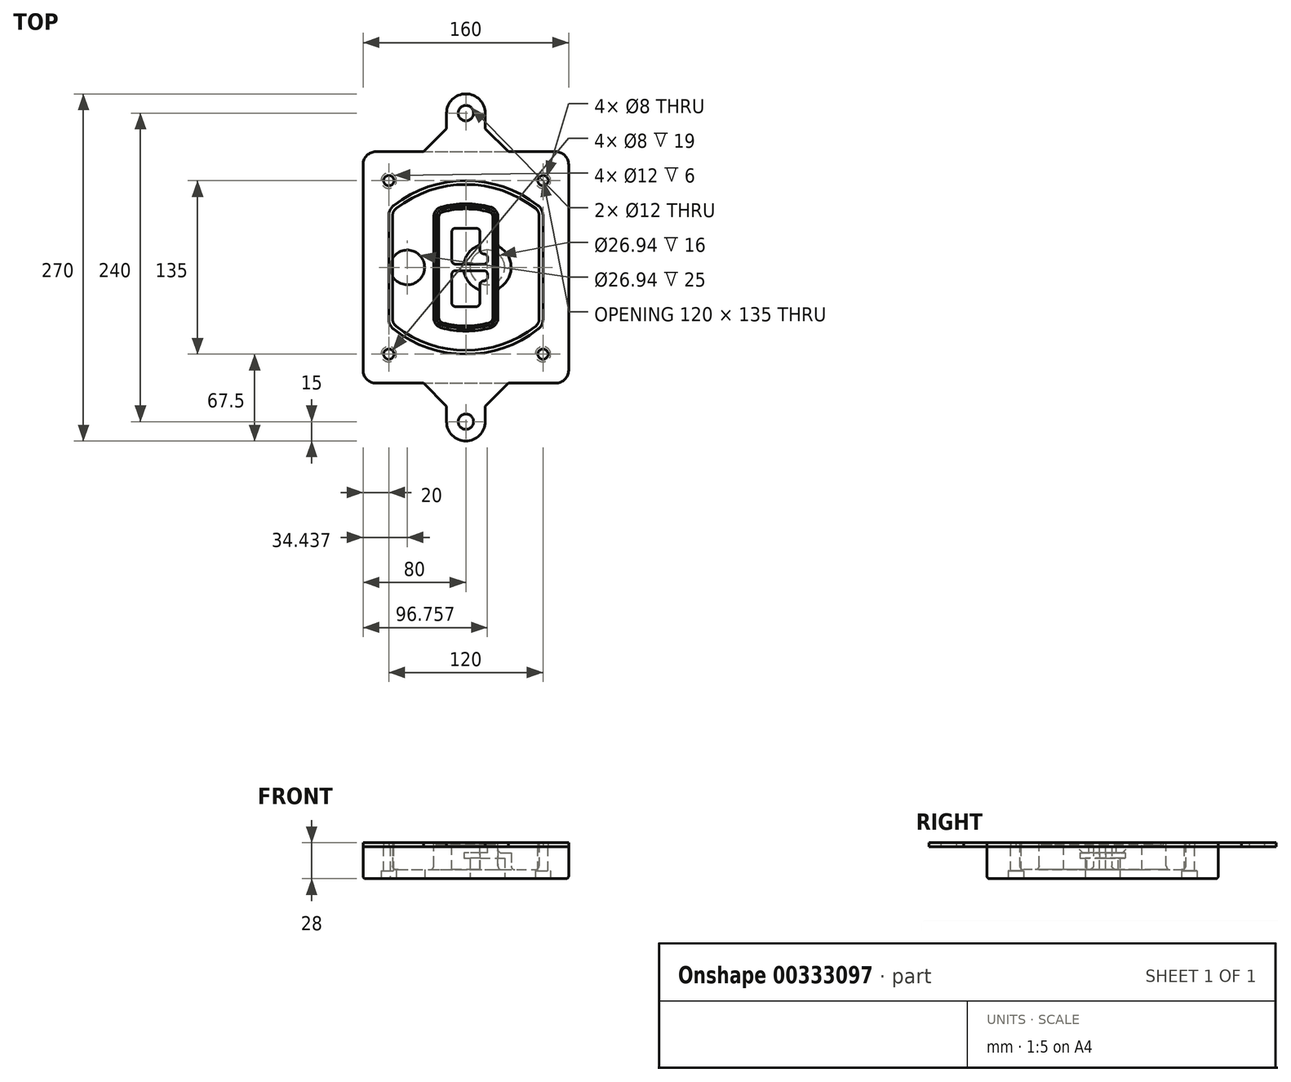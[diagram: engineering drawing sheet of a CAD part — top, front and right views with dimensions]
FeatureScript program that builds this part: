
annotation { "Feature Type Name" : "Feature", "Feature Type Description" : "" }
export const myFeature = defineFeature(function(context is Context, id is Id, definition is map)
    precondition{}
    {
        {
            var Q0;
            Q0=qCreatedBy(makeId("Top.planeOp"),FACE);
            var sketch = newSketch(context, id + "F0", { "sketchPlane" : qUnion([Q0])});
            skPoint(sketch, "E0.rect.middle", {"position": v(0, 0) * mm});
            skLineSegment(sketch, "E1.bottom", {"start": v(-70, -90) * mm, "end": v(70, -90) * mm});
            skLineSegment(sketch, "E1.top", {"start": v(-70, 90) * mm, "end": v(70, 90) * mm});
            skLineSegment(sketch, "E1.left", {"start": v(-80, -80) * mm, "end": v(-80, 80) * mm});
            skLineSegment(sketch, "E1.right", {"start": v(80, -80) * mm, "end": v(80, 80) * mm});
            skLineSegment(sketch, "E2", {"start": v(-80, 90) * mm, "end": v(80, -90) * mm, "construction": true});
            skLineSegment(sketch, "E3", {"start": v(80, 90) * mm, "end": v(-80, -90) * mm, "construction": true});
            skCircle(sketch, "E4", {"center": v(-60, 67.5) * mm, "radius": 4 * mm});
            skCircle(sketch, "E5", {"center": v(60, 67.5) * mm, "radius": 4 * mm});
            skCircle(sketch, "E6", {"center": v(60, -67.5) * mm, "radius": 4 * mm});
            skCircle(sketch, "E7", {"center": v(-60, -67.5) * mm, "radius": 4 * mm});
            skLineSegment(sketch, "E8", {"start": v(-60, 67.5) * mm, "end": v(60, 67.5) * mm, "construction": true});
            skLineSegment(sketch, "E9", {"start": v(60, 67.5) * mm, "end": v(60, -67.5) * mm, "construction": true});
            skLineSegment(sketch, "E10", {"start": v(60, -67.5) * mm, "end": v(-60, -67.5) * mm, "construction": true});
            skLineSegment(sketch, "E11", {"start": v(-60, -67.5) * mm, "end": v(-60, 67.5) * mm, "construction": true});
            skLineSegment(sketch, "E12", {"start": v(-60, 40.3) * mm, "end": v(-60, -40.3) * mm});
            skLineSegment(sketch, "E13", {"start": v(60, 40.3) * mm, "end": v(60, -40.3) * mm});
            skArc(sketch, "E14", {"start": v(56.15, 48.18) * mm, "mid": v(0, 67.5) * mm, "end": v(-56.15, 48.18) * mm});
            skArc(sketch, "E15", {"start": v(-56.15, -48.18) * mm, "mid": v(0, -67.5) * mm, "end": v(56.15, -48.18) * mm});
            skLineSegment(sketch, "E16", {"start": v(-60, 0) * mm, "end": v(60, 0) * mm, "construction": true});
            skPoint(sketch, "E17.visualSharp", {"position": v(-60, -45) * mm});
            skArc(sketch, "E17.filletArc", {"start": v(-60, -40.3) * mm, "mid": v(-58.99, -44.68) * mm, "end": v(-56.15, -48.18) * mm});
            skPoint(sketch, "E18.visualSharp", {"position": v(-60, 45) * mm});
            skArc(sketch, "E18.filletArc", {"start": v(-56.15, 48.18) * mm, "mid": v(-58.99, 44.68) * mm, "end": v(-60, 40.3) * mm});
            skPoint(sketch, "E19.visualSharp", {"position": v(60, 45) * mm});
            skArc(sketch, "E19.filletArc", {"start": v(60, 40.3) * mm, "mid": v(58.99, 44.68) * mm, "end": v(56.15, 48.18) * mm});
            skPoint(sketch, "E20.visualSharp", {"position": v(60, -45) * mm});
            skArc(sketch, "E20.filletArc", {"start": v(56.15, -48.18) * mm, "mid": v(58.99, -44.68) * mm, "end": v(60, -40.3) * mm});
            skPoint(sketch, "E21.visualSharp", {"position": v(-80, 90) * mm});
            skArc(sketch, "E21.filletArc", {"start": v(-70, 90) * mm, "mid": v(-77.07, 87.07) * mm, "end": v(-80, 80) * mm});
            skPoint(sketch, "E22.visualSharp", {"position": v(80, 90) * mm});
            skArc(sketch, "E22.filletArc", {"start": v(80, 80) * mm, "mid": v(77.07, 87.07) * mm, "end": v(70, 90) * mm});
            skPoint(sketch, "E23.visualSharp", {"position": v(80, -90) * mm});
            skArc(sketch, "E23.filletArc", {"start": v(70, -90) * mm, "mid": v(77.07, -87.07) * mm, "end": v(80, -80) * mm});
            skPoint(sketch, "E24.visualSharp", {"position": v(-80, -90) * mm});
            skArc(sketch, "E24.filletArc", {"start": v(-80, -80) * mm, "mid": v(-77.07, -87.07) * mm, "end": v(-70, -90) * mm});
            skArc(sketch, "E25.0", {"start": v(57, 40.3) * mm, "mid": v(56.3, 43.36) * mm, "end": v(54.3, 45.81) * mm});
            skLineSegment(sketch, "E25.1", {"start": v(57, 40.3) * mm, "end": v(57, -40.3) * mm});
            skArc(sketch, "E25.2", {"start": v(54.3, -45.81) * mm, "mid": v(56.3, -43.36) * mm, "end": v(57, -40.3) * mm});
            skArc(sketch, "E25.3", {"start": v(-54.3, -45.81) * mm, "mid": v(0, -64.5) * mm, "end": v(54.3, -45.81) * mm});
            skArc(sketch, "E25.4", {"start": v(-57, -40.3) * mm, "mid": v(-56.3, -43.36) * mm, "end": v(-54.3, -45.81) * mm});
            skArc(sketch, "E25.5", {"start": v(54.3, 45.81) * mm, "mid": v(0, 64.5) * mm, "end": v(-54.3, 45.81) * mm});
            skLineSegment(sketch, "E25.6", {"start": v(-57, 40.3) * mm, "end": v(-57, -40.3) * mm});
            skArc(sketch, "E25.7", {"start": v(-54.3, 45.81) * mm, "mid": v(-56.3, 43.36) * mm, "end": v(-57, 40.3) * mm});
            skArc(sketch, "E26.0", {"start": v(-58.62, 51.33) * mm, "mid": v(-62.58, 46.43) * mm, "end": v(-64, 40.3) * mm});
            skArc(sketch, "E26.1", {"start": v(58.62, 51.33) * mm, "mid": v(0, 71.5) * mm, "end": v(-58.62, 51.33) * mm});
            skArc(sketch, "E26.2", {"start": v(64, 40.3) * mm, "mid": v(62.58, 46.43) * mm, "end": v(58.62, 51.33) * mm});
            skLineSegment(sketch, "E26.3", {"start": v(64, 40.3) * mm, "end": v(64, -40.3) * mm});
            skArc(sketch, "E26.4", {"start": v(58.62, -51.33) * mm, "mid": v(62.58, -46.43) * mm, "end": v(64, -40.3) * mm});
            skLineSegment(sketch, "E26.5", {"start": v(-64, 40.3) * mm, "end": v(-64, -40.3) * mm});
            skArc(sketch, "E26.6", {"start": v(-58.62, -51.33) * mm, "mid": v(0, -71.5) * mm, "end": v(58.62, -51.33) * mm});
            skArc(sketch, "E26.7", {"start": v(-64, -40.3) * mm, "mid": v(-62.58, -46.43) * mm, "end": v(-58.62, -51.33) * mm});
            skSolve(sketch);
        }
        {
            var Q0;
            Q0=makeQuery(id+"F0.imprint","IMPRINT",FACE,{"disambiguationData":[TD([[makeQuery(id+"F0.imprint","IMPRINT",EDGE,{"derivedFrom":sQuery(id+"F0.wireOp",EDGE,"E1.bottom")}),1.0]])]});
            var Q1;
            Q1=makeQuery(id+"F0.imprint","IMPRINT",FACE,{"disambiguationData":[TD([[makeQuery(id+"F0.imprint","IMPRINT",EDGE,{"derivedFrom":sQuery(id+"F0.wireOp",EDGE,"E12")}),1.0]])]});
            var Q2;
            Q2=makeQuery(id+"F0.imprint","IMPRINT",FACE,{"disambiguationData":[TD([[makeQuery(id+"F0.imprint","IMPRINT",EDGE,{"derivedFrom":sQuery(id+"F0.wireOp",EDGE,"E25.0")}),1.0]])]});
            var Q3;
            Q3=makeQuery(id+"F0.imprint","IMPRINT",FACE,{"disambiguationData":[TD([[makeQuery(id+"F0.imprint","IMPRINT",EDGE,{"derivedFrom":sQuery(id+"F0.wireOp",EDGE,"E12")}),-1.0]])]});
            extrude(context, id + "F1", {"entities" : qUnion([Q0, Q1, Q2, Q3]), "oppositeDirection" : true, "depth" : 25 * mm});
        }
        {
            var Q0;
            Q0=makeQuery(id+"F0.imprint","IMPRINT",FACE,{"disambiguationData":[TD([[makeQuery(id+"F0.imprint","IMPRINT",EDGE,{"derivedFrom":sQuery(id+"F0.wireOp",EDGE,"E12")}),1.0]])]});
            extrude(context, id + "F2", {"entities" : qUnion([Q0]), "operationType" : NewBodyOperationType.ADD, "depth" : 3 * mm});
        }
        {
            var Q0;
            Q0=makeQuery(id+"F0.imprint","IMPRINT",FACE,{"disambiguationData":[TD([[makeQuery(id+"F0.imprint","IMPRINT",EDGE,{"derivedFrom":sQuery(id+"F0.wireOp",EDGE,"E25.0")}),1.0]])]});
            extrude(context, id + "F3", {"entities" : qUnion([Q0]), "operationType" : NewBodyOperationType.REMOVE, "oppositeDirection" : true, "depth" : 18 * mm});
        }
        {
            var Q0;
            Q0=makeQuery(id+"F2.opExtrude","CAP_FACE",FACE,{"disambiguationData":[OSD([sQuery(id+"F0.wireOp",EDGE,"E12"),sQuery(id+"F0.wireOp",EDGE,"E13"),sQuery(id+"F0.wireOp",EDGE,"E14"),sQuery(id+"F0.wireOp",EDGE,"E15"),sQuery(id+"F0.wireOp",EDGE,"E17.filletArc"),sQuery(id+"F0.wireOp",EDGE,"E18.filletArc"),sQuery(id+"F0.wireOp",EDGE,"E19.filletArc"),sQuery(id+"F0.wireOp",EDGE,"E20.filletArc"),sQuery(id+"F0.wireOp",EDGE,"E25.0"),sQuery(id+"F0.wireOp",EDGE,"E25.1"),sQuery(id+"F0.wireOp",EDGE,"E25.2"),sQuery(id+"F0.wireOp",EDGE,"E25.3"),sQuery(id+"F0.wireOp",EDGE,"E25.4"),sQuery(id+"F0.wireOp",EDGE,"E25.5"),sQuery(id+"F0.wireOp",EDGE,"E25.6"),sQuery(id+"F0.wireOp",EDGE,"E25.7")])],"isStart":false});
            var sketch = newSketch(context, id + "F4", { "sketchPlane" : qUnion([Q0])});
            skArc(sketch, "E27.0", {"start": v(-19.08, -46.97) * mm, "mid": v(0, -49.5) * mm, "end": v(19.08, -46.97) * mm});
            skArc(sketch, "E28.0", {"start": v(19.08, 46.97) * mm, "mid": v(0, 49.5) * mm, "end": v(-19.08, 46.97) * mm});
            skLineSegment(sketch, "E29", {"start": v(-25, 39.25) * mm, "end": v(-25, -39.25) * mm});
            skLineSegment(sketch, "E30", {"start": v(25, 39.25) * mm, "end": v(25, -39.25) * mm});
            skLineSegment(sketch, "E31", {"start": v(-25, 45.1) * mm, "end": v(25, 45.1) * mm, "construction": true});
            skLineSegment(sketch, "E32", {"start": v(-25, -45.1) * mm, "end": v(25, -45.1) * mm, "construction": true});
            skPoint(sketch, "E33.visualSharp", {"position": v(-25, 45.1) * mm});
            skArc(sketch, "E33.filletArc", {"start": v(-19.08, 46.97) * mm, "mid": v(-23.35, 44.11) * mm, "end": v(-25, 39.25) * mm});
            skPoint(sketch, "E34.visualSharp", {"position": v(25, 45.1) * mm});
            skArc(sketch, "E34.filletArc", {"start": v(25, 39.25) * mm, "mid": v(23.35, 44.11) * mm, "end": v(19.08, 46.97) * mm});
            skPoint(sketch, "E35.visualSharp", {"position": v(25, -45.1) * mm});
            skArc(sketch, "E35.filletArc", {"start": v(19.08, -46.97) * mm, "mid": v(23.35, -44.11) * mm, "end": v(25, -39.25) * mm});
            skPoint(sketch, "E36.visualSharp", {"position": v(-25, -45.1) * mm});
            skArc(sketch, "E36.filletArc", {"start": v(-25, -39.25) * mm, "mid": v(-23.35, -44.11) * mm, "end": v(-19.08, -46.97) * mm});
            skArc(sketch, "E37.0", {"start": v(54.3, 45.81) * mm, "mid": v(0, 64.5) * mm, "end": v(-54.3, 45.81) * mm});
            skArc(sketch, "E37.1", {"start": v(-54.3, 45.81) * mm, "mid": v(-56.3, 43.36) * mm, "end": v(-57, 40.3) * mm});
            skLineSegment(sketch, "E37.2", {"start": v(-57, 40.3) * mm, "end": v(-57, -40.3) * mm});
            skArc(sketch, "E37.3", {"start": v(-57, -40.3) * mm, "mid": v(-56.3, -43.36) * mm, "end": v(-54.3, -45.81) * mm});
            skArc(sketch, "E37.4", {"start": v(-54.3, -45.81) * mm, "mid": v(0, -64.5) * mm, "end": v(54.3, -45.81) * mm});
            skArc(sketch, "E37.5", {"start": v(54.3, -45.81) * mm, "mid": v(56.3, -43.36) * mm, "end": v(57, -40.3) * mm});
            skLineSegment(sketch, "E37.6", {"start": v(57, 40.3) * mm, "end": v(57, -40.3) * mm});
            skArc(sketch, "E37.7", {"start": v(57, 40.3) * mm, "mid": v(56.3, 43.36) * mm, "end": v(54.3, 45.81) * mm});
            skLineSegment(sketch, "E38.0", {"start": v(23, 39.25) * mm, "end": v(23, -39.25) * mm});
            skArc(sketch, "E38.1", {"start": v(18.56, -45.04) * mm, "mid": v(21.76, -42.9) * mm, "end": v(23, -39.25) * mm});
            skArc(sketch, "E38.2", {"start": v(-18.56, -45.04) * mm, "mid": v(0, -47.5) * mm, "end": v(18.56, -45.04) * mm});
            skArc(sketch, "E38.3", {"start": v(-23, -39.25) * mm, "mid": v(-21.76, -42.9) * mm, "end": v(-18.56, -45.04) * mm});
            skLineSegment(sketch, "E38.4", {"start": v(-23, 39.25) * mm, "end": v(-23, -39.25) * mm});
            skArc(sketch, "E38.5", {"start": v(23, 39.25) * mm, "mid": v(21.76, 42.9) * mm, "end": v(18.56, 45.04) * mm});
            skArc(sketch, "E38.6", {"start": v(-18.56, 45.04) * mm, "mid": v(-21.76, 42.9) * mm, "end": v(-23, 39.25) * mm});
            skArc(sketch, "E38.7", {"start": v(18.56, 45.04) * mm, "mid": v(0, 47.5) * mm, "end": v(-18.56, 45.04) * mm});
            skArc(sketch, "E39.0", {"start": v(21, 39.25) * mm, "mid": v(20.18, 41.68) * mm, "end": v(18.04, 43.1) * mm});
            skLineSegment(sketch, "E39.1", {"start": v(21, 39.25) * mm, "end": v(21, -39.25) * mm});
            skArc(sketch, "E39.2", {"start": v(18.04, -43.1) * mm, "mid": v(20.18, -41.68) * mm, "end": v(21, -39.25) * mm});
            skArc(sketch, "E39.3", {"start": v(-18.04, -43.1) * mm, "mid": v(0, -45.5) * mm, "end": v(18.04, -43.1) * mm});
            skArc(sketch, "E39.4", {"start": v(-21, -39.25) * mm, "mid": v(-20.18, -41.68) * mm, "end": v(-18.04, -43.1) * mm});
            skArc(sketch, "E39.5", {"start": v(18.04, 43.1) * mm, "mid": v(0, 45.5) * mm, "end": v(-18.04, 43.1) * mm});
            skLineSegment(sketch, "E39.6", {"start": v(-21, 39.25) * mm, "end": v(-21, -39.25) * mm});
            skArc(sketch, "E39.7", {"start": v(-18.04, 43.1) * mm, "mid": v(-20.18, 41.68) * mm, "end": v(-21, 39.25) * mm});
            skLineSegment(sketch, "E40", {"start": v(-25, 0) * mm, "end": v(25, 0) * mm, "construction": true});
            skLineSegment(sketch, "E41", {"start": v(-11, 5.5) * mm, "end": v(-11, 27.5) * mm});
            skLineSegment(sketch, "E42", {"start": v(-8, 30.5) * mm, "end": v(8, 30.5) * mm});
            skLineSegment(sketch, "E43", {"start": v(11, 27.5) * mm, "end": v(11, 13.5) * mm});
            skLineSegment(sketch, "E44", {"start": v(14, 10.5) * mm, "end": v(14, 10.5) * mm});
            skLineSegment(sketch, "E45", {"start": v(17, 7.5) * mm, "end": v(17, 5.5) * mm});
            skLineSegment(sketch, "E46", {"start": v(14, 2.5) * mm, "end": v(-8, 2.5) * mm});
            skPoint(sketch, "E47.visualSharp", {"position": v(-11, 30.5) * mm});
            skArc(sketch, "E47.filletArc", {"start": v(-8, 30.5) * mm, "mid": v(-10.12, 29.62) * mm, "end": v(-11, 27.5) * mm});
            skPoint(sketch, "E48.visualSharp", {"position": v(11, 30.5) * mm});
            skArc(sketch, "E48.filletArc", {"start": v(11, 27.5) * mm, "mid": v(10.12, 29.62) * mm, "end": v(8, 30.5) * mm});
            skPoint(sketch, "E49.visualSharp", {"position": v(11, 10.5) * mm});
            skArc(sketch, "E49.filletArc", {"start": v(11, 13.5) * mm, "mid": v(11.88, 11.38) * mm, "end": v(14, 10.5) * mm});
            skPoint(sketch, "E50.visualSharp", {"position": v(17, 10.5) * mm});
            skArc(sketch, "E50.filletArc", {"start": v(17, 7.5) * mm, "mid": v(16.12, 9.62) * mm, "end": v(14, 10.5) * mm});
            skPoint(sketch, "E51.visualSharp", {"position": v(17, 2.5) * mm});
            skArc(sketch, "E51.filletArc", {"start": v(14, 2.5) * mm, "mid": v(16.12, 3.38) * mm, "end": v(17, 5.5) * mm});
            skPoint(sketch, "E52.visualSharp", {"position": v(-11, 2.5) * mm});
            skArc(sketch, "E52.filletArc", {"start": v(-11, 5.5) * mm, "mid": v(-10.12, 3.38) * mm, "end": v(-8, 2.5) * mm});
            skLineSegment(sketch, "E53.0.MirrorCS", {"start": v(14, -2.5) * mm, "end": v(-8, -2.5) * mm});
            skArc(sketch, "E54.0.MirrorCS", {"start": v(-11, -5.5) * mm, "mid": v(-10.12, -3.38) * mm, "end": v(-8, -2.5) * mm});
            skLineSegment(sketch, "E55.0.MirrorCS", {"start": v(-11, -5.5) * mm, "end": v(-11, -27.5) * mm});
            skArc(sketch, "E56.0.MirrorCS", {"start": v(-8, -30.5) * mm, "mid": v(-10.12, -29.62) * mm, "end": v(-11, -27.5) * mm});
            skLineSegment(sketch, "E57.0.MirrorCS", {"start": v(-8, -30.5) * mm, "end": v(8, -30.5) * mm});
            skArc(sketch, "E58.0.MirrorCS", {"start": v(11, -27.5) * mm, "mid": v(10.12, -29.62) * mm, "end": v(8, -30.5) * mm});
            skLineSegment(sketch, "E59.0.MirrorCS", {"start": v(11, -27.5) * mm, "end": v(11, -13.5) * mm});
            skArc(sketch, "E60.0.MirrorCS", {"start": v(11, -13.5) * mm, "mid": v(11.88, -11.38) * mm, "end": v(14, -10.5) * mm});
            skArc(sketch, "E61.0.MirrorCS", {"start": v(17, -7.5) * mm, "mid": v(16.12, -9.62) * mm, "end": v(14, -10.5) * mm});
            skLineSegment(sketch, "E62.0.MirrorCS", {"start": v(17, -7.5) * mm, "end": v(17, -5.5) * mm});
            skArc(sketch, "E63.0.MirrorCS", {"start": v(14, -2.5) * mm, "mid": v(16.12, -3.38) * mm, "end": v(17, -5.5) * mm});
            skSolve(sketch);
        }
        {
            var Q0;
            Q0=makeQuery(id+"F4.imprint","IMPRINT",FACE,{"disambiguationData":[TD([[makeQuery(id+"F4.imprint","IMPRINT",EDGE,{"derivedFrom":sQuery(id+"F4.wireOp",EDGE,"E27.0")}),1.0]])]});
            var Q1;
            Q1=makeQuery(id+"F4.imprint","IMPRINT",FACE,{"disambiguationData":[TD([[makeQuery(id+"F4.imprint","IMPRINT",EDGE,{"derivedFrom":sQuery(id+"F4.wireOp",EDGE,"E38.0")}),-1.0]])]});
            var Q2;
            Q2=makeQuery(id+"F4.imprint","IMPRINT",FACE,{"disambiguationData":[TD([[makeQuery(id+"F4.imprint","IMPRINT",EDGE,{"derivedFrom":sQuery(id+"F4.wireOp",EDGE,"E39.0")}),1.0]])]});
            extrude(context, id + "F5", {"entities" : qUnion([Q0, Q1, Q2]), "operationType" : NewBodyOperationType.ADD, "endBound" : BoundingType.UP_TO_NEXT, "oppositeDirection" : true, "depth" : 25 * mm});
        }
        {
            var Q0;
            Q0=makeQuery(id+"F4.imprint","IMPRINT",FACE,{"disambiguationData":[TD([[makeQuery(id+"F4.imprint","IMPRINT",EDGE,{"derivedFrom":sQuery(id+"F4.wireOp",EDGE,"E38.0")}),-1.0]])]});
            extrude(context, id + "F6", {"entities" : qUnion([Q0]), "operationType" : NewBodyOperationType.REMOVE, "oppositeDirection" : true, "depth" : 2 * mm});
        }
        {
            var Q0;
            Q0=makeQuery(id+"F1.opExtrude","CAP_FACE",FACE,{"disambiguationData":[OSD([sQuery(id+"F0.wireOp",EDGE,"E1.bottom"),sQuery(id+"F0.wireOp",EDGE,"E1.top"),sQuery(id+"F0.wireOp",EDGE,"E1.left"),sQuery(id+"F0.wireOp",EDGE,"E1.right"),sQuery(id+"F0.wireOp",EDGE,"E4"),sQuery(id+"F0.wireOp",EDGE,"E5"),sQuery(id+"F0.wireOp",EDGE,"E6"),sQuery(id+"F0.wireOp",EDGE,"E7"),sQuery(id+"F0.wireOp",EDGE,"E21.filletArc"),sQuery(id+"F0.wireOp",EDGE,"E22.filletArc"),sQuery(id+"F0.wireOp",EDGE,"E23.filletArc"),sQuery(id+"F0.wireOp",EDGE,"E24.filletArc")])],"isStart":false});
            var sketch = newSketch(context, id + "F7", { "sketchPlane" : qUnion([Q0])});
            skCircle(sketch, "E64", {"center": v(16.76, 0) * mm, "radius": 13.47 * mm});
            skCircle(sketch, "E65", {"center": v(-45.56, 0) * mm, "radius": 13.47 * mm});
            skLineSegment(sketch, "E66", {"start": v(80, 0) * mm, "end": v(-80, 0) * mm});
            skCircle(sketch, "E67", {"center": v(16.76, 0) * mm, "radius": 18.47 * mm});
            skCircle(sketch, "E68", {"center": v(60, -67.5) * mm, "radius": 6 * mm});
            skCircle(sketch, "E69", {"center": v(-60, -67.5) * mm, "radius": 6 * mm});
            skCircle(sketch, "E70", {"center": v(-60, 67.5) * mm, "radius": 6 * mm});
            skCircle(sketch, "E71", {"center": v(60, 67.5) * mm, "radius": 6 * mm});
            skSolve(sketch);
        }
        {
            var Q0;
            {var subQ1=sQuery(id+"F7.wireOp",EDGE,"E66");var subQ4=sQuery(id+"F7.wireOp",EDGE,"E64");var subQ6=makeQuery(id+"F7.imprint","INTERSECT",VERTEX,{"disambiguationData":[OD(0.0)],"derivedFrom":[subQ4,subQ1]});Q0=makeQuery(id+"F7.imprint","IMPRINT",FACE,{"disambiguationData":[TD([[makeQuery(id+"F7.imprint","IMPRINT",EDGE,{"disambiguationData":[TD([[subQ6,-1.0]])],"derivedFrom":subQ4}),-1.0]])]});}
            var Q1;
            {var subQ0=sQuery(id+"F7.wireOp",EDGE,"E66");var subQ1=sQuery(id+"F7.wireOp",EDGE,"E64");var subQ3=makeQuery(id+"F7.imprint","INTERSECT",VERTEX,{"disambiguationData":[OD(0.0)],"derivedFrom":[subQ1,subQ0]});Q1=makeQuery(id+"F7.imprint","IMPRINT",FACE,{"disambiguationData":[TD([[makeQuery(id+"F7.imprint","IMPRINT",EDGE,{"disambiguationData":[TD([[subQ3,-1.0]])],"derivedFrom":subQ1}),1.0]])]});}
            var Q2;
            {var subQ0=sQuery(id+"F7.wireOp",EDGE,"E66");var subQ1=sQuery(id+"F7.wireOp",EDGE,"E64");var subQ3=makeQuery(id+"F7.imprint","INTERSECT",VERTEX,{"disambiguationData":[OD(0.0)],"derivedFrom":[subQ1,subQ0]});Q2=makeQuery(id+"F7.imprint","IMPRINT",FACE,{"disambiguationData":[TD([[makeQuery(id+"F7.imprint","IMPRINT",EDGE,{"disambiguationData":[TD([[subQ3,1.0]])],"derivedFrom":subQ1}),1.0]])]});}
            var Q3;
            {var subQ1=sQuery(id+"F7.wireOp",EDGE,"E66");var subQ4=sQuery(id+"F7.wireOp",EDGE,"E64");var subQ6=makeQuery(id+"F7.imprint","INTERSECT",VERTEX,{"disambiguationData":[OD(0.0)],"derivedFrom":[subQ4,subQ1]});Q3=makeQuery(id+"F7.imprint","IMPRINT",FACE,{"disambiguationData":[TD([[makeQuery(id+"F7.imprint","IMPRINT",EDGE,{"disambiguationData":[TD([[subQ6,1.0]])],"derivedFrom":subQ4}),-1.0]])]});}
            extrude(context, id + "F8", {"entities" : qUnion([Q0, Q1, Q2, Q3]), "operationType" : NewBodyOperationType.ADD, "oppositeDirection" : true, "depth" : 20 * mm});
        }
        {
            var Q0;
            {var subQ0=sQuery(id+"F7.wireOp",EDGE,"E66");var subQ1=sQuery(id+"F7.wireOp",EDGE,"E64");var subQ3=makeQuery(id+"F7.imprint","INTERSECT",VERTEX,{"disambiguationData":[OD(0.0)],"derivedFrom":[subQ1,subQ0]});Q0=makeQuery(id+"F7.imprint","IMPRINT",FACE,{"disambiguationData":[TD([[makeQuery(id+"F7.imprint","IMPRINT",EDGE,{"disambiguationData":[TD([[subQ3,-1.0]])],"derivedFrom":subQ1}),1.0]])]});}
            var Q1;
            {var subQ0=sQuery(id+"F7.wireOp",EDGE,"E66");var subQ1=sQuery(id+"F7.wireOp",EDGE,"E64");var subQ3=makeQuery(id+"F7.imprint","INTERSECT",VERTEX,{"disambiguationData":[OD(0.0)],"derivedFrom":[subQ1,subQ0]});Q1=makeQuery(id+"F7.imprint","IMPRINT",FACE,{"disambiguationData":[TD([[makeQuery(id+"F7.imprint","IMPRINT",EDGE,{"disambiguationData":[TD([[subQ3,1.0]])],"derivedFrom":subQ1}),1.0]])]});}
            extrude(context, id + "F9", {"entities" : qUnion([Q0, Q1]), "operationType" : NewBodyOperationType.REMOVE, "oppositeDirection" : true, "depth" : 16 * mm});
        }
        {
            var Q0;
            {var subQ0=sQuery(id+"F7.wireOp",EDGE,"E66");var subQ1=sQuery(id+"F7.wireOp",EDGE,"E65");var subQ3=makeQuery(id+"F7.imprint","INTERSECT",VERTEX,{"disambiguationData":[OD(0.0)],"derivedFrom":[subQ1,subQ0]});Q0=makeQuery(id+"F7.imprint","IMPRINT",FACE,{"disambiguationData":[TD([[makeQuery(id+"F7.imprint","IMPRINT",EDGE,{"disambiguationData":[TD([[subQ3,-1.0]])],"derivedFrom":subQ1}),1.0]])]});}
            var Q1;
            {var subQ0=sQuery(id+"F7.wireOp",EDGE,"E66");var subQ1=sQuery(id+"F7.wireOp",EDGE,"E65");var subQ3=makeQuery(id+"F7.imprint","INTERSECT",VERTEX,{"disambiguationData":[OD(0.0)],"derivedFrom":[subQ1,subQ0]});Q1=makeQuery(id+"F7.imprint","IMPRINT",FACE,{"disambiguationData":[TD([[makeQuery(id+"F7.imprint","IMPRINT",EDGE,{"disambiguationData":[TD([[subQ3,1.0]])],"derivedFrom":subQ1}),1.0]])]});}
            extrude(context, id + "F10", {"entities" : qUnion([Q0, Q1]), "operationType" : NewBodyOperationType.REMOVE, "oppositeDirection" : true, "depth" : 25 * mm});
        }
        {
            var Q0;
            Q0=makeQuery(id+"F7.imprint","IMPRINT",FACE,{"disambiguationData":[TD([[makeQuery(id+"F7.imprint","IMPRINT",EDGE,{"derivedFrom":sQuery(id+"F7.wireOp",EDGE,"E68")}),1.0]])]});
            var Q1;
            Q1=makeQuery(id+"F7.imprint","IMPRINT",FACE,{"disambiguationData":[TD([[makeQuery(id+"F7.imprint","IMPRINT",EDGE,{"derivedFrom":makeQuery(id+"F1.opExtrude","CAP_EDGE",EDGE,{"disambiguationData":[OSD([sQuery(id+"F0.wireOp",EDGE,"E5")])],"isStart":false})}),-1.0]])]});
            var Q2;
            Q2=makeQuery(id+"F7.imprint","IMPRINT",FACE,{"disambiguationData":[TD([[makeQuery(id+"F7.imprint","IMPRINT",EDGE,{"derivedFrom":sQuery(id+"F7.wireOp",EDGE,"E69")}),1.0]])]});
            var Q3;
            Q3=makeQuery(id+"F7.imprint","IMPRINT",FACE,{"disambiguationData":[TD([[makeQuery(id+"F7.imprint","IMPRINT",EDGE,{"derivedFrom":makeQuery(id+"F1.opExtrude","CAP_EDGE",EDGE,{"disambiguationData":[OSD([sQuery(id+"F0.wireOp",EDGE,"E4")])],"isStart":false})}),-1.0]])]});
            var Q4;
            Q4=makeQuery(id+"F7.imprint","IMPRINT",FACE,{"disambiguationData":[TD([[makeQuery(id+"F7.imprint","IMPRINT",EDGE,{"derivedFrom":sQuery(id+"F7.wireOp",EDGE,"E70")}),1.0]])]});
            var Q5;
            Q5=makeQuery(id+"F7.imprint","IMPRINT",FACE,{"disambiguationData":[TD([[makeQuery(id+"F7.imprint","IMPRINT",EDGE,{"derivedFrom":makeQuery(id+"F1.opExtrude","CAP_EDGE",EDGE,{"disambiguationData":[OSD([sQuery(id+"F0.wireOp",EDGE,"E7")])],"isStart":false})}),-1.0]])]});
            var Q6;
            Q6=makeQuery(id+"F7.imprint","IMPRINT",FACE,{"disambiguationData":[TD([[makeQuery(id+"F7.imprint","IMPRINT",EDGE,{"derivedFrom":sQuery(id+"F7.wireOp",EDGE,"E71")}),1.0]])]});
            var Q7;
            Q7=makeQuery(id+"F7.imprint","IMPRINT",FACE,{"disambiguationData":[TD([[makeQuery(id+"F7.imprint","IMPRINT",EDGE,{"derivedFrom":makeQuery(id+"F1.opExtrude","CAP_EDGE",EDGE,{"disambiguationData":[OSD([sQuery(id+"F0.wireOp",EDGE,"E6")])],"isStart":false})}),-1.0]])]});
            extrude(context, id + "F11", {"entities" : qUnion([Q0, Q1, Q2, Q3, Q4, Q5, Q6, Q7]), "operationType" : NewBodyOperationType.REMOVE, "oppositeDirection" : true, "depth" : 6 * mm});
        }
        {
            var Q0;
            Q0=makeQuery(id+"F9.boolean.opBoolean","COPY",FACE,{"derivedFrom":makeQuery(id+"F9.opExtrude","CAP_FACE",FACE,{"disambiguationData":[OSD([sQuery(id+"F7.wireOp",EDGE,"E64")])],"isStart":false})});
            var sketch = newSketch(context, id + "F12", { "sketchPlane" : qUnion([Q0])});
            skArc(sketch, "E72.0", {"start": v(11, 17.55) * mm, "mid": v(2.57, 11.82) * mm, "end": v(-1.54, 2.5) * mm});
            skArc(sketch, "E72.1", {"start": v(-1.54, -2.5) * mm, "mid": v(2.57, -11.82) * mm, "end": v(11, -17.55) * mm});
            skLineSegment(sketch, "E73", {"start": v(-1.54, -2.5) * mm, "end": v(14, -2.5) * mm});
            skLineSegment(sketch, "E74.0", {"start": v(14, 2.5) * mm, "end": v(-1.54, 2.5) * mm});
            skArc(sketch, "E74.1", {"start": v(14, 2.5) * mm, "mid": v(16.12, 3.38) * mm, "end": v(17, 5.5) * mm});
            skLineSegment(sketch, "E74.2", {"start": v(17, 7.5) * mm, "end": v(17, 5.5) * mm});
            skArc(sketch, "E74.3", {"start": v(17, 7.5) * mm, "mid": v(16.12, 9.62) * mm, "end": v(14, 10.5) * mm});
            skArc(sketch, "E74.4", {"start": v(11, 13.5) * mm, "mid": v(11.88, 11.38) * mm, "end": v(14, 10.5) * mm});
            skLineSegment(sketch, "E74.5", {"start": v(11, 17.55) * mm, "end": v(11, 13.5) * mm});
            skLineSegment(sketch, "E74.7", {"start": v(14, -2.5) * mm, "end": v(-1.54, -2.5) * mm});
            skArc(sketch, "E74.8", {"start": v(14, -2.5) * mm, "mid": v(16.12, -3.38) * mm, "end": v(17, -5.5) * mm});
            skLineSegment(sketch, "E74.9", {"start": v(17, -7.5) * mm, "end": v(17, -5.5) * mm});
            skArc(sketch, "E74.10", {"start": v(17, -7.5) * mm, "mid": v(16.12, -9.62) * mm, "end": v(14, -10.5) * mm});
            skArc(sketch, "E74.11", {"start": v(11, -13.5) * mm, "mid": v(11.88, -11.38) * mm, "end": v(14, -10.5) * mm});
            skLineSegment(sketch, "E74.12", {"start": v(11, -17.55) * mm, "end": v(11, -13.5) * mm});
            skPoint(sketch, "E75.orphan", {"position": v(11, -27.5) * mm});
            skPoint(sketch, "E76.orphan", {"position": v(-8, -2.5) * mm});
            skPoint(sketch, "E77.orphan", {"position": v(-8, 2.5) * mm});
            skPoint(sketch, "E78.orphan", {"position": v(11, 27.5) * mm});
            skSolve(sketch);
        }
        {
            var Q0;
            {var subQ7=sQuery(id+"F12.wireOp",EDGE,"E72.0");var subQ14=sQuery(id+"F12.wireOp",EDGE,"E72.1");var subQ16=sQuery(id+"F12.wireOp",EDGE,"E74.1");var subQ18=sQuery(id+"F12.wireOp",EDGE,"E74.8");Q0=qUnion([makeQuery(id+"F12.imprint","IMPRINT",FACE,{"disambiguationData":[TD([[makeQuery(id+"F12.imprint","IMPRINT",EDGE,{"derivedFrom":subQ7}),1.0]])]}),makeQuery(id+"F12.imprint","IMPRINT",FACE,{"disambiguationData":[TD([[makeQuery(id+"F12.imprint","IMPRINT",EDGE,{"derivedFrom":subQ14}),1.0]])]}),makeQuery(id+"F12.imprint","IMPRINT",FACE,{"disambiguationData":[TD([[makeQuery(id+"F12.imprint","IMPRINT",EDGE,{"derivedFrom":subQ16}),1.0]])]}),makeQuery(id+"F12.imprint","IMPRINT",FACE,{"disambiguationData":[TD([[makeQuery(id+"F12.imprint","IMPRINT",EDGE,{"derivedFrom":subQ18}),-1.0]])]})]);}
            var Q1;
            Q1=makeQuery(id+"F5.boolean.opBoolean","SPLIT",FACE,{"disambiguationData":[TD([makeQuery(id+"F5.opExtrude","SWEPT_FACE",FACE,{"disambiguationData":[OSD([sQuery(id+"F4.wireOp",EDGE,"E41")])]})])],"derivedFrom":makeQuery(id+"F3.boolean.opBoolean","COPY",FACE,{"derivedFrom":makeQuery(id+"F3.opExtrude","CAP_FACE",FACE,{"disambiguationData":[OSD([sQuery(id+"F0.wireOp",EDGE,"E25.0"),sQuery(id+"F0.wireOp",EDGE,"E25.1"),sQuery(id+"F0.wireOp",EDGE,"E25.2"),sQuery(id+"F0.wireOp",EDGE,"E25.3"),sQuery(id+"F0.wireOp",EDGE,"E25.4"),sQuery(id+"F0.wireOp",EDGE,"E25.5"),sQuery(id+"F0.wireOp",EDGE,"E25.6"),sQuery(id+"F0.wireOp",EDGE,"E25.7")])],"isStart":false})})});
            extrude(context, id + "F13", {"entities" : qUnion([Q0]), "operationType" : NewBodyOperationType.REMOVE, "endBound" : BoundingType.UP_TO_SURFACE, "endBoundEntityFace" : qUnion([Q1]), "depth" : 25 * mm});
        }
        {
            var Q0;
            Q0=makeQuery(id+"F3.boolean.opBoolean","COPY",EDGE,{"derivedFrom":makeQuery(id+"F3.opExtrude","CAP_EDGE",EDGE,{"disambiguationData":[OSD([sQuery(id+"F0.wireOp",EDGE,"E25.6")])],"isStart":false})});
            var Q1;
            Q1=makeQuery(id+"F8.boolean.opBoolean","INTERSECT",EDGE,{"derivedFrom":[makeQuery(id+"F5.opExtrude","SWEPT_FACE",FACE,{"disambiguationData":[OSD([sQuery(id+"F4.wireOp",EDGE,"E30")])]}),makeQuery(id+"F8.opExtrude","CAP_FACE",FACE,{"disambiguationData":[OSD([sQuery(id+"F7.wireOp",EDGE,"E67")])],"isStart":false})]});
            var Q2;
            Q2=makeQuery(id+"F8.boolean.opBoolean","INTERSECT",EDGE,{"disambiguationData":[OD(1.0)],"derivedFrom":[makeQuery(id+"F5.opExtrude","SWEPT_FACE",FACE,{"disambiguationData":[OSD([sQuery(id+"F4.wireOp",EDGE,"E30")])]}),makeQuery(id+"F8.opExtrude","SWEPT_FACE",FACE,{"disambiguationData":[OSD([sQuery(id+"F7.wireOp",EDGE,"E67")])]})]});
            var Q3;
            {var subQ0=sQuery(id+"F4.wireOp",EDGE,"E30");Q3=makeQuery(id+"F8.boolean.opBoolean","SPLIT",EDGE,{"disambiguationData":[TD([makeQuery(id+"F5.opExtrude","SWEPT_FACE",FACE,{"disambiguationData":[OSD([sQuery(id+"F4.wireOp",EDGE,"E35.filletArc")])]})])],"derivedFrom":makeQuery(id+"F5.opExtrude","CAP_EDGE",EDGE,{"disambiguationData":[OSD([subQ0])],"isStart":false})});}
            var Q4;
            {var subQ0=sQuery(id+"F0.wireOp",EDGE,"E25.7");var subQ1=sQuery(id+"F0.wireOp",EDGE,"E25.1");var subQ2=sQuery(id+"F0.wireOp",EDGE,"E25.6");var subQ3=sQuery(id+"F0.wireOp",EDGE,"E25.5");var subQ4=sQuery(id+"F0.wireOp",EDGE,"E25.4");var subQ5=sQuery(id+"F0.wireOp",EDGE,"E25.0");var subQ6=sQuery(id+"F0.wireOp",EDGE,"E25.2");var subQ7=sQuery(id+"F0.wireOp",EDGE,"E25.3");Q4=makeQuery(id+"F8.boolean.opBoolean","INTERSECT",EDGE,{"derivedFrom":[makeQuery(id+"F5.boolean.opBoolean","SPLIT",FACE,{"disambiguationData":[TD([makeQuery(id+"F2.opExtrude","SWEPT_FACE",FACE,{"disambiguationData":[OSD([subQ5])]})])],"derivedFrom":makeQuery(id+"F3.boolean.opBoolean","COPY",FACE,{"derivedFrom":makeQuery(id+"F3.opExtrude","CAP_FACE",FACE,{"disambiguationData":[OSD([subQ5,subQ1,subQ6,subQ7,subQ4,subQ3,subQ2,subQ0])],"isStart":false})})}),makeQuery(id+"F8.opExtrude","SWEPT_FACE",FACE,{"disambiguationData":[OSD([sQuery(id+"F7.wireOp",EDGE,"E67")])]})]});}
            var Q5;
            Q5=makeQuery(id+"F8.boolean.opBoolean","INTERSECT",EDGE,{"disambiguationData":[OD(0.0)],"derivedFrom":[makeQuery(id+"F5.opExtrude","SWEPT_FACE",FACE,{"disambiguationData":[OSD([sQuery(id+"F4.wireOp",EDGE,"E30")])]}),makeQuery(id+"F8.opExtrude","SWEPT_FACE",FACE,{"disambiguationData":[OSD([sQuery(id+"F7.wireOp",EDGE,"E67")])]})]});
            fillet(context, id + "F14", {"entities" : qUnion([Q0, Q1, Q2, Q3, Q4, Q5]), "radius" : 3 * mm, "tangentPropagation" : true, "allowEdgeOverflow" : false});
        }
        {
            var Q0;
            Q0=makeQuery(id+"F1.opExtrude","CAP_EDGE",EDGE,{"disambiguationData":[OSD([sQuery(id+"F0.wireOp",EDGE,"E1.bottom")])],"isStart":false});
            fillet(context, id + "F15", {"entities" : qUnion([Q0]), "radius" : 2 * mm, "tangentPropagation" : true, "allowEdgeOverflow" : false});
        }
        {
            var Q0;
            {var subQ0=sQuery(id+"F0.wireOp",EDGE,"E21.filletArc");var subQ1=sQuery(id+"F0.wireOp",EDGE,"E7");var subQ2=sQuery(id+"F0.wireOp",EDGE,"E6");var subQ3=sQuery(id+"F0.wireOp",EDGE,"E5");var subQ4=sQuery(id+"F0.wireOp",EDGE,"E4");var subQ5=sQuery(id+"F0.wireOp",EDGE,"E22.filletArc");var subQ6=sQuery(id+"F0.wireOp",EDGE,"E1.bottom");var subQ7=sQuery(id+"F0.wireOp",EDGE,"E1.right");var subQ8=sQuery(id+"F0.wireOp",EDGE,"E1.top");var subQ9=sQuery(id+"F0.wireOp",EDGE,"E1.left");var subQ10=sQuery(id+"F0.wireOp",EDGE,"E23.filletArc");var subQ11=sQuery(id+"F0.wireOp",EDGE,"E24.filletArc");Q0=makeQuery(id+"F2.boolean.opBoolean","SPLIT",FACE,{"disambiguationData":[TD([makeQuery(id+"F1.opExtrude","SWEPT_FACE",FACE,{"disambiguationData":[OSD([subQ6])]})])],"derivedFrom":makeQuery(id+"F1.opExtrude","CAP_FACE",FACE,{"disambiguationData":[OSD([subQ6,subQ8,subQ9,subQ7,subQ4,subQ3,subQ2,subQ1,subQ0,subQ5,subQ10,subQ11])],"isStart":true})});}
            var sketch = newSketch(context, id + "F16", { "sketchPlane" : qUnion([Q0])});
            skLineSegment(sketch, "E79", {"start": v(0, 90) * mm, "end": v(0, 120) * mm, "construction": true});
            skLineSegment(sketch, "E80", {"start": v(-33, 90) * mm, "end": v(-15, 108) * mm});
            skLineSegment(sketch, "E81", {"start": v(-15, 108) * mm, "end": v(-15, 120) * mm});
            skLineSegment(sketch, "E82.MirrorCS", {"start": v(15, 108) * mm, "end": v(15, 120) * mm});
            skLineSegment(sketch, "E83.MirrorCS", {"start": v(33, 90) * mm, "end": v(15, 108) * mm});
            skCircle(sketch, "E84", {"center": v(0, 120) * mm, "radius": 6 * mm});
            skArc(sketch, "E85", {"start": v(15, 120) * mm, "mid": v(0, 135) * mm, "end": v(-15, 120) * mm});
            skLineSegment(sketch, "E86", {"start": v(-80, 0) * mm, "end": v(80, 0) * mm, "construction": true});
            skLineSegment(sketch, "E87.MirrorCS", {"start": v(33, -90) * mm, "end": v(15, -108) * mm});
            skLineSegment(sketch, "E88.MirrorCS", {"start": v(15, -108) * mm, "end": v(15, -120) * mm});
            skArc(sketch, "E89.MirrorCS", {"start": v(15, -120) * mm, "mid": v(0, -135) * mm, "end": v(-15, -120) * mm});
            skCircle(sketch, "E90.MirrorC", {"center": v(0, -120) * mm, "radius": 6 * mm});
            skLineSegment(sketch, "E91.MirrorCS", {"start": v(0, -90) * mm, "end": v(0, -120) * mm, "construction": true});
            skLineSegment(sketch, "E92.MirrorCS", {"start": v(-15, -108) * mm, "end": v(-15, -120) * mm});
            skLineSegment(sketch, "E93.MirrorCS", {"start": v(-33, -90) * mm, "end": v(-15, -108) * mm});
            skSolve(sketch);
        }
        {
            var Q0;
            Q0=makeQuery(id+"F16.imprint","IMPRINT",FACE,{"disambiguationData":[TD([[makeQuery(id+"F16.imprint","IMPRINT",EDGE,{"derivedFrom":makeQuery(id+"F1.opExtrude","CAP_EDGE",EDGE,{"disambiguationData":[OSD([sQuery(id+"F0.wireOp",EDGE,"E1.left")])],"isStart":true})}),-1.0]])]});
            var Q1;
            {var subQ1=sQuery(id+"F16.wireOp",EDGE,"E80");Q1=makeQuery(id+"F16.imprint","IMPRINT",FACE,{"disambiguationData":[TD([[makeQuery(id+"F16.imprint","IMPRINT",EDGE,{"derivedFrom":subQ1}),-1.0]])]});}
            var Q2;
            {var subQ0=sQuery(id+"F16.wireOp",EDGE,"E87.MirrorCS");Q2=makeQuery(id+"F16.imprint","IMPRINT",FACE,{"disambiguationData":[TD([[makeQuery(id+"F16.imprint","IMPRINT",EDGE,{"derivedFrom":subQ0}),-1.0]])]});}
            var Q3;
            Q3=makeQuery(id+"F2.opExtrude","CAP_FACE",FACE,{"disambiguationData":[OSD([sQuery(id+"F0.wireOp",EDGE,"E12"),sQuery(id+"F0.wireOp",EDGE,"E13"),sQuery(id+"F0.wireOp",EDGE,"E14"),sQuery(id+"F0.wireOp",EDGE,"E15"),sQuery(id+"F0.wireOp",EDGE,"E17.filletArc"),sQuery(id+"F0.wireOp",EDGE,"E18.filletArc"),sQuery(id+"F0.wireOp",EDGE,"E19.filletArc"),sQuery(id+"F0.wireOp",EDGE,"E20.filletArc"),sQuery(id+"F0.wireOp",EDGE,"E25.0"),sQuery(id+"F0.wireOp",EDGE,"E25.1"),sQuery(id+"F0.wireOp",EDGE,"E25.2"),sQuery(id+"F0.wireOp",EDGE,"E25.3"),sQuery(id+"F0.wireOp",EDGE,"E25.4"),sQuery(id+"F0.wireOp",EDGE,"E25.5"),sQuery(id+"F0.wireOp",EDGE,"E25.6"),sQuery(id+"F0.wireOp",EDGE,"E25.7")])],"isStart":false});
            extrude(context, id + "F17", {"entities" : qUnion([Q0, Q1, Q2]), "endBound" : BoundingType.UP_TO_SURFACE, "endBoundEntityFace" : qUnion([Q3]), "depth" : 25 * mm});
        }
    });
